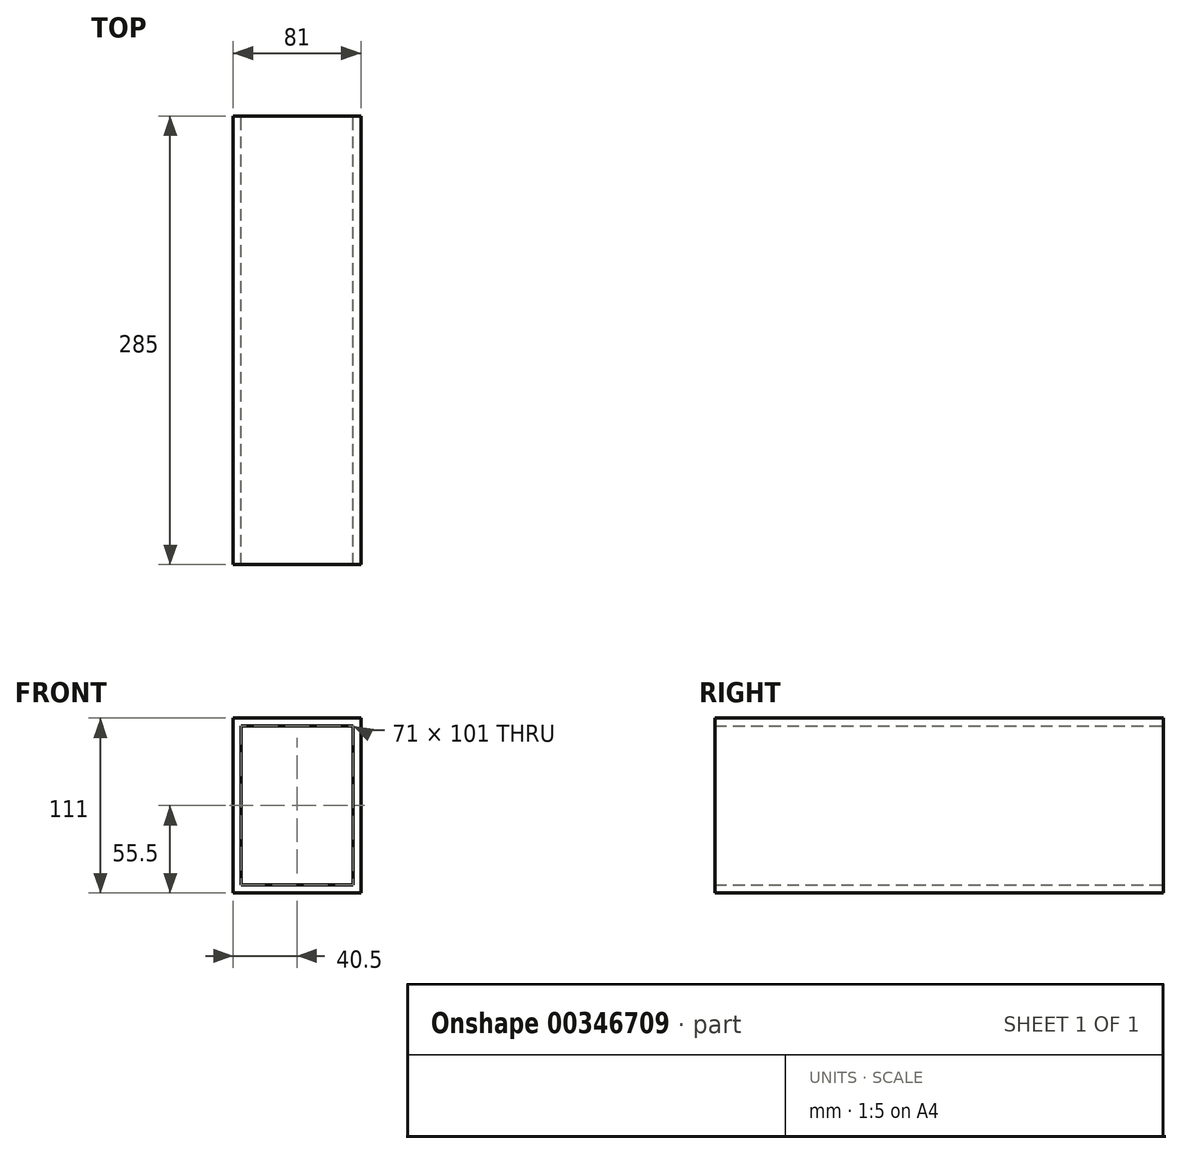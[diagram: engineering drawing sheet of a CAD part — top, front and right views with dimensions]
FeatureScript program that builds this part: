
annotation { "Feature Type Name" : "Feature", "Feature Type Description" : "" }
export const myFeature = defineFeature(function(context is Context, id is Id, definition is map)
    precondition{}
    {
        {
            var Q0;
            Q0=qCreatedBy(makeId("Front.planeOp"),FACE);
            var sketch = newSketch(context, id + "F0", { "sketchPlane" : qUnion([Q0])});
            skLineSegment(sketch, "E0.bottom", {"start": v(35.5, -50.5) * mm, "end": v(-35.5, -50.5) * mm});
            skLineSegment(sketch, "E0.top", {"start": v(35.5, 50.5) * mm, "end": v(-35.5, 50.5) * mm});
            skLineSegment(sketch, "E0.left", {"start": v(35.5, -50.5) * mm, "end": v(35.5, 50.5) * mm});
            skLineSegment(sketch, "E0.right", {"start": v(-35.5, -50.5) * mm, "end": v(-35.5, 50.5) * mm});
            skPoint(sketch, "E0.middle", {"position": v(0, 0) * mm});
            skLineSegment(sketch, "E1.0", {"start": v(-40.5, -55.5) * mm, "end": v(-40.5, 55.5) * mm});
            skLineSegment(sketch, "E1.1", {"start": v(40.5, -55.5) * mm, "end": v(-40.5, -55.5) * mm});
            skLineSegment(sketch, "E1.2", {"start": v(40.5, -55.5) * mm, "end": v(40.5, 55.5) * mm});
            skLineSegment(sketch, "E1.3", {"start": v(40.5, 55.5) * mm, "end": v(-40.5, 55.5) * mm});
            skSolve(sketch);
        }
        {
            var Q0;
            Q0 = qSketchRegion(id + "F0", true);
            extrude(context, id + "F1", {"entities" : qUnion([Q0]), "depth" : 285 * mm});
        }
    });
